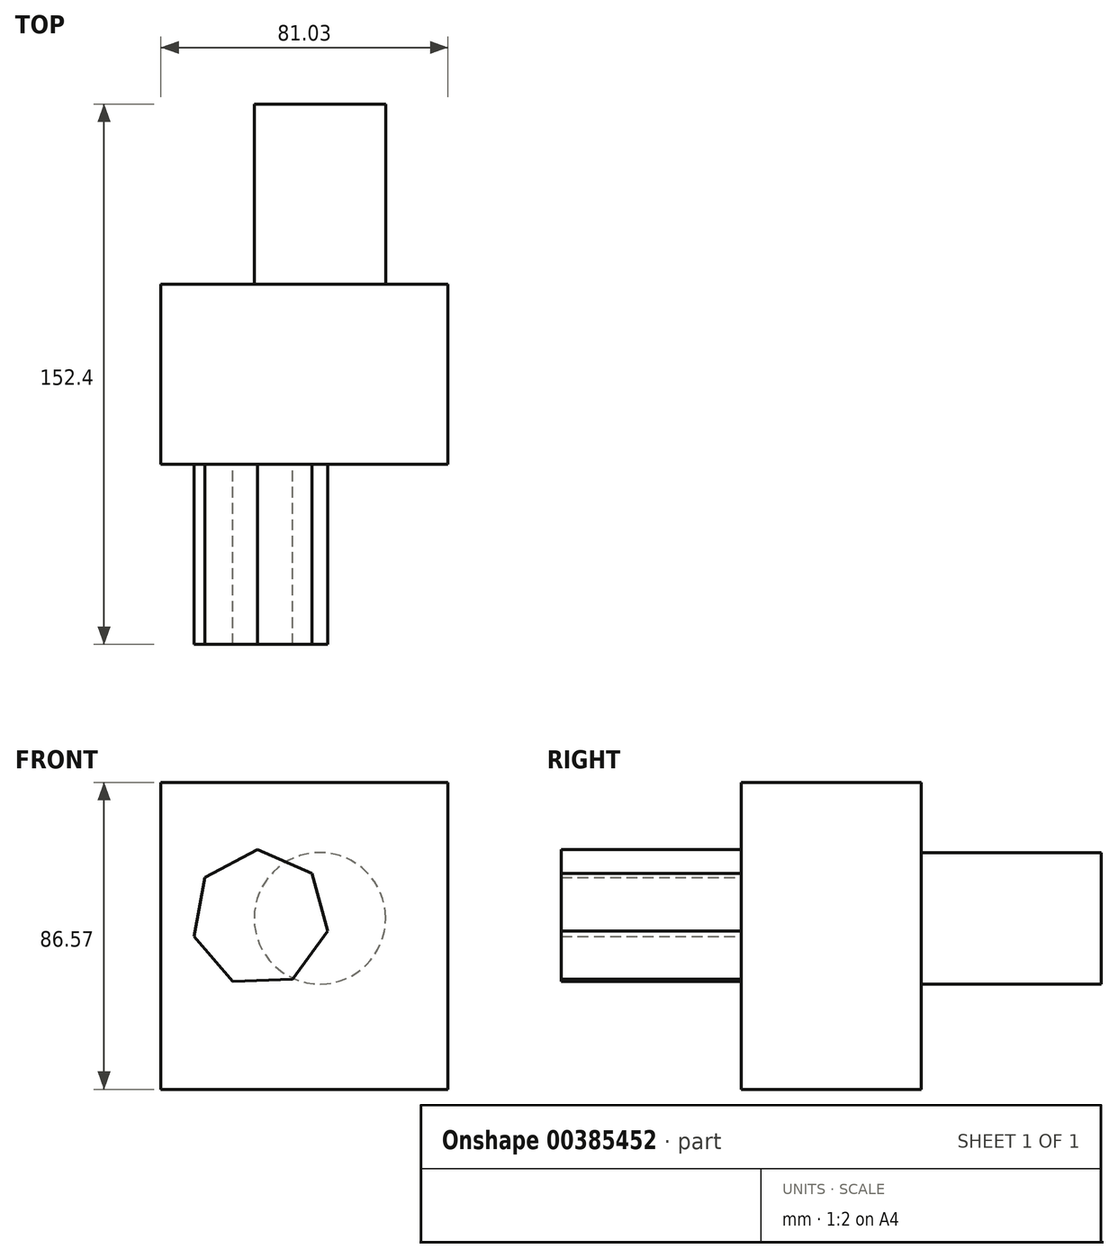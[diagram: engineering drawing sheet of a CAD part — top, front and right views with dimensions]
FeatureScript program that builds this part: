
annotation { "Feature Type Name" : "Feature", "Feature Type Description" : "" }
export const myFeature = defineFeature(function(context is Context, id is Id, definition is map)
    precondition{}
    {
        {
            var Q0;
            Q0=qCreatedBy(makeId("Front.planeOp"),FACE);
            var sketch = newSketch(context, id + "F0", { "sketchPlane" : qUnion([Q0])});
            skLineSegment(sketch, "E0.bottom", {"start": v(-44.89, 38.33) * mm, "end": v(36.14, 38.33) * mm});
            skLineSegment(sketch, "E0.top", {"start": v(-44.89, -48.24) * mm, "end": v(36.14, -48.24) * mm});
            skLineSegment(sketch, "E0.left", {"start": v(-44.89, 38.33) * mm, "end": v(-44.89, -48.24) * mm});
            skLineSegment(sketch, "E0.right", {"start": v(36.14, 38.33) * mm, "end": v(36.14, -48.24) * mm});
            skSolve(sketch);
        }
        {
            var Q0;
            Q0 = qSketchRegion(id + "F0", true);
            extrude(context, id + "F1", {"entities" : qUnion([Q0]), "depth" : 25.4 * mm});
        }
        {
            var Q0;
            Q0=qCreatedBy(makeId("Front.planeOp"),FACE);
            var sketch = newSketch(context, id + "F2", { "sketchPlane" : qUnion([Q0])});
            skCircle(sketch, "E1", {"center": v(0, 0) * mm, "radius": 18.54 * mm});
            skSolve(sketch);
        }
        {
            var Q0;
            Q0 = qSketchRegion(id + "F2", true);
            var Q1;
            Q1=makeQuery(id+"F1.opExtrude","CAP_FACE",FACE,{"disambiguationData":[OSD([sQuery(id+"F0.wireOp",EDGE,"E0.bottom"),sQuery(id+"F0.wireOp",EDGE,"E0.top"),sQuery(id+"F0.wireOp",EDGE,"E0.left"),sQuery(id+"F0.wireOp",EDGE,"E0.right")])],"isStart":false});
            extrude(context, id + "F3", {"entities" : qUnion([Q0, Q1]), "operationType" : NewBodyOperationType.ADD, "oppositeDirection" : true, "depth" : 25.4 * mm});
        }
        {
            var Q0;
            Q0=makeQuery(id+"F3.opExtrude","CAP_FACE",FACE,{"disambiguationData":[OSD([sQuery(id+"F2.wireOp",EDGE,"E1")])],"isStart":false});
            extrude(context, id + "F4", {"entities" : qUnion([Q0]), "operationType" : NewBodyOperationType.ADD, "depth" : 25.4 * mm});
        }
        {
            var Q0;
            Q0=makeQuery(id+"F1.opExtrude","CAP_FACE",FACE,{"disambiguationData":[OSD([sQuery(id+"F0.wireOp",EDGE,"E0.bottom"),sQuery(id+"F0.wireOp",EDGE,"E0.top"),sQuery(id+"F0.wireOp",EDGE,"E0.left"),sQuery(id+"F0.wireOp",EDGE,"E0.right")])],"isStart":false});
            extrude(context, id + "F5", {"entities" : qUnion([Q0]), "operationType" : NewBodyOperationType.ADD, "depth" : 25.4 * mm});
        }
        {
            var Q0;
            Q0=makeQuery(id+"F5.opExtrude","CAP_FACE",FACE,{"disambiguationData":[OSD([sQuery(id+"F0.wireOp",EDGE,"E0.bottom"),sQuery(id+"F0.wireOp",EDGE,"E0.top"),sQuery(id+"F0.wireOp",EDGE,"E0.left"),sQuery(id+"F0.wireOp",EDGE,"E0.right")])],"isStart":false});
            var sketch = newSketch(context, id + "F6", { "sketchPlane" : qUnion([Q0])});
            skCircle(sketch, "E2.cCircle", {"center": v(-16.86, 0) * mm, "radius": 17.46 * mm, "construction": true});
            skLineSegment(sketch, "E2.0", {"start": v(-2.2, 12.67) * mm, "end": v(2.2, -3.57) * mm});
            skLineSegment(sketch, "E2.1", {"start": v(2.2, -3.57) * mm, "end": v(-7.77, -17.12) * mm});
            skLineSegment(sketch, "E2.2", {"start": v(-7.77, -17.12) * mm, "end": v(-24.58, -17.78) * mm});
            skLineSegment(sketch, "E2.3", {"start": v(-24.58, -17.78) * mm, "end": v(-35.57, -5.05) * mm});
            skLineSegment(sketch, "E2.4", {"start": v(-35.57, -5.05) * mm, "end": v(-32.48, 11.48) * mm});
            skLineSegment(sketch, "E2.5", {"start": v(-32.48, 11.48) * mm, "end": v(-17.62, 19.37) * mm});
            skLineSegment(sketch, "E2.6", {"start": v(-17.62, 19.37) * mm, "end": v(-2.2, 12.67) * mm});
            skPoint(sketch, "E2.0.midPoint", {"position": v(0, 4.55) * mm});
            skSolve(sketch);
        }
        {
            var Q0;
            Q0=makeQuery(id+"F6.imprint","IMPRINT",FACE,{"disambiguationData":[TD([[makeQuery(id+"F6.imprint","IMPRINT",EDGE,{"derivedFrom":sQuery(id+"F6.wireOp",EDGE,"E2.0")}),-1.0]])]});
            extrude(context, id + "F7", {"entities" : qUnion([Q0]), "operationType" : NewBodyOperationType.ADD, "depth" : 50.8 * mm});
        }
    });
